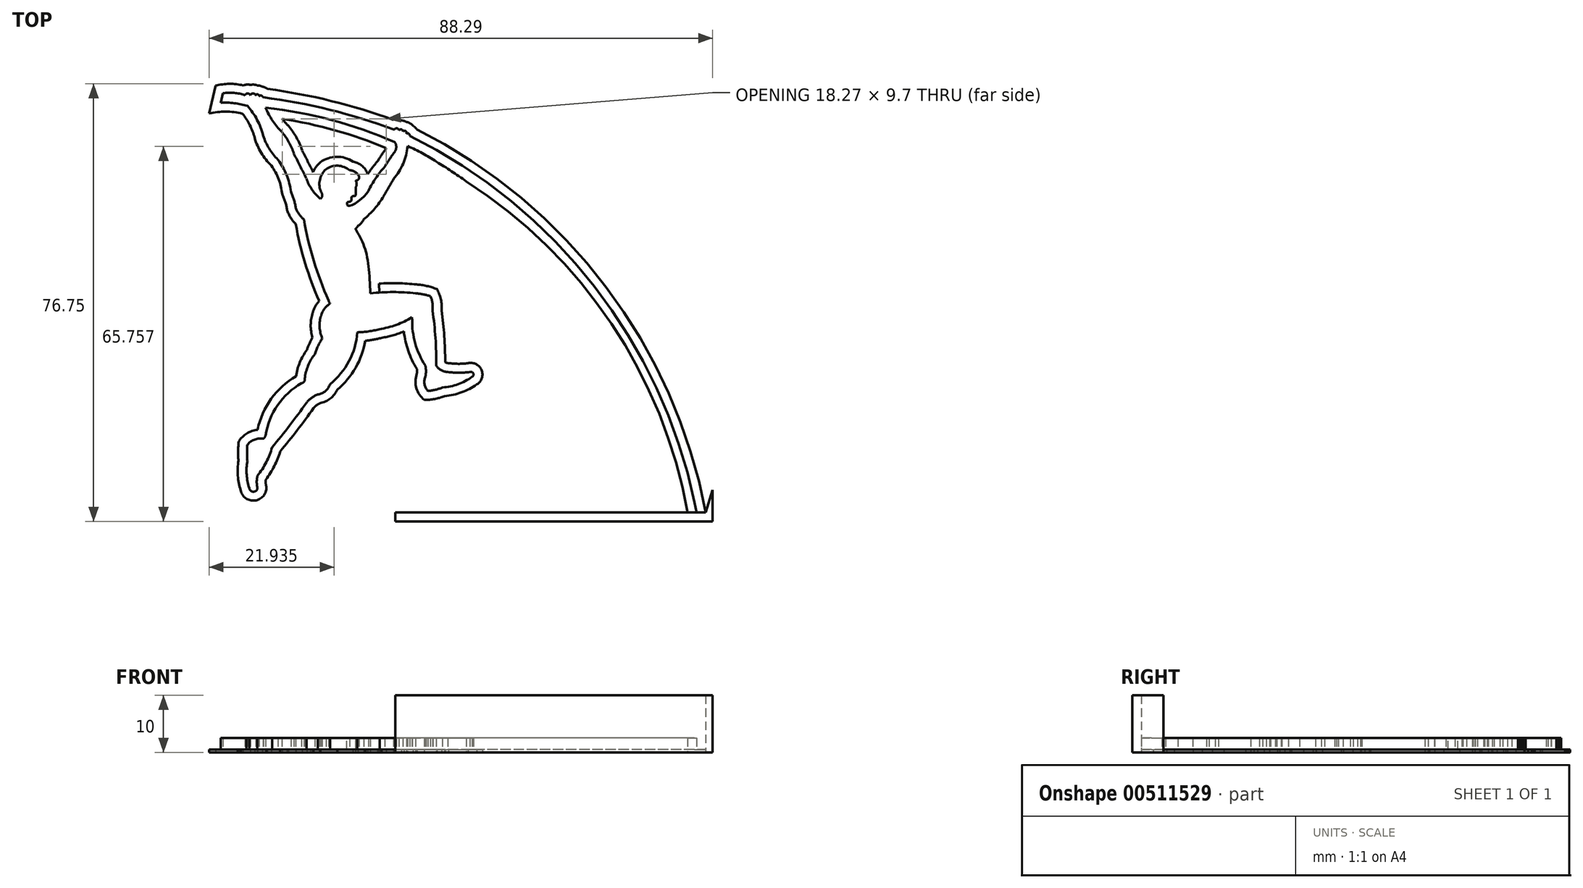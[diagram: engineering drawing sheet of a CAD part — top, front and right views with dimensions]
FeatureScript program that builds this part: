
annotation { "Feature Type Name" : "Feature", "Feature Type Description" : "" }
export const myFeature = defineFeature(function(context is Context, id is Id, definition is map)
    precondition{}
    {
        {
            var Q0;
            Q0=qCreatedBy(makeId("Top.planeOp"),FACE);
            var sketch = newSketch(context, id + "F0", { "sketchPlane" : qUnion([Q0])});
            skArc(sketch, "E0", {"start": v(-35.16, 43.56) * mm, "mid": v(-37.47, 44.04) * mm, "end": v(-39.82, 44.1) * mm});
            skArc(sketch, "E1", {"start": v(-35.6, 45.44) * mm, "mid": v(-37.5, 45.84) * mm, "end": v(-39.44, 45.77) * mm});
            skArc(sketch, "E2", {"start": v(-9.39, 39.38) * mm, "mid": v(-20.75, 42.89) * mm, "end": v(-32.43, 45.06) * mm});
            skArc(sketch, "E3", {"start": v(-9.38, 37.25) * mm, "mid": v(-20.44, 41.08) * mm, "end": v(-31.94, 43.24) * mm});
            skLineSegment(sketch, "E4", {"start": v(-39.82, 44.1) * mm, "end": v(-39.44, 45.77) * mm});
            skArc(sketch, "E5", {"start": v(43.25, -25.95) * mm, "mid": v(25.65, 11.92) * mm, "end": v(-6.7, 38.32) * mm});
            skArc(sketch, "E6", {"start": v(-33.7, 45.44) * mm, "mid": v(-34.17, 45.73) * mm, "end": v(-34.65, 45.44) * mm});
            skArc(sketch, "E7", {"start": v(-33.1, 45.27) * mm, "mid": v(-33.33, 45.57) * mm, "end": v(-33.7, 45.44) * mm});
            skArc(sketch, "E8", {"start": v(-32.43, 45.06) * mm, "mid": v(-32.7, 45.37) * mm, "end": v(-33.1, 45.27) * mm});
            skArc(sketch, "E9", {"start": v(-34.65, 45.44) * mm, "mid": v(-35.12, 45.73) * mm, "end": v(-35.6, 45.44) * mm});
            skArc(sketch, "E10", {"start": v(-32.38, 38.34) * mm, "mid": v(-33.46, 41.11) * mm, "end": v(-35.16, 43.56) * mm});
            skArc(sketch, "E11", {"start": v(-32.38, 38.34) * mm, "mid": v(-31.35, 36.06) * mm, "end": v(-29.8, 34.1) * mm});
            skArc(sketch, "E12", {"start": v(-31.94, 43.24) * mm, "mid": v(-30.76, 40.97) * mm, "end": v(-29.12, 39) * mm});
            skArc(sketch, "E13", {"start": v(-27, 35.16) * mm, "mid": v(-27.88, 37.18) * mm, "end": v(-29.12, 39) * mm});
            skArc(sketch, "E14", {"start": v(-24.81, 30.82) * mm, "mid": v(-25.9, 32.99) * mm, "end": v(-27, 35.16) * mm});
            skArc(sketch, "E15", {"start": v(-24.81, 30.82) * mm, "mid": v(-23.82, 28.85) * mm, "end": v(-22.34, 27.22) * mm});
            skArc(sketch, "E16", {"start": v(-27.53, 28.5) * mm, "mid": v(-28.29, 31.45) * mm, "end": v(-29.8, 34.1) * mm});
            skArc(sketch, "E17", {"start": v(-26.66, 25.66) * mm, "mid": v(-27, 27.1) * mm, "end": v(-27.53, 28.5) * mm});
            skArc(sketch, "E18", {"start": v(-26.66, 25.66) * mm, "mid": v(-26.1, 24.55) * mm, "end": v(-25.24, 23.63) * mm});
            skArc(sketch, "E19", {"start": v(-22.34, 27.22) * mm, "mid": v(-22.04, 27.8) * mm, "end": v(-22.22, 28.43) * mm});
            skArc(sketch, "E20", {"start": v(-21.38, 32.44) * mm, "mid": v(-22.46, 30.58) * mm, "end": v(-22.22, 28.43) * mm});
            skArc(sketch, "E21", {"start": v(-17.24, 32.26) * mm, "mid": v(-19.28, 33.06) * mm, "end": v(-21.38, 32.44) * mm});
            skArc(sketch, "E22", {"start": v(-15.57, 31.17) * mm, "mid": v(-16.24, 31.96) * mm, "end": v(-17.24, 32.26) * mm});
            skArc(sketch, "E23", {"start": v(-16.16, 30.45) * mm, "mid": v(-15.68, 30.66) * mm, "end": v(-15.57, 31.17) * mm});
            skArc(sketch, "E24", {"start": v(-16.16, 29.27) * mm, "mid": v(-16, 29.86) * mm, "end": v(-16.16, 30.45) * mm});
            skLineSegment(sketch, "E25", {"start": v(-16.16, 29.27) * mm, "end": v(-16.16, 28.39) * mm});
            skFitSpline(sketch, "E26", {"points": [v(-16.16, 28.39) * mm, v(-16.24, 27.77) * mm, v(-16.82, 27.66) * mm, v(-17.03, 26.84) * mm, v(-17.62, 26.64) * mm, v(-17.5, 26.04) * mm, v(-13.93, 28.66) * mm], "startDerivative": vector(-0.04, -4.98) * mm, "endDerivative": vector(6, 10.29) * mm});
            skArc(sketch, "E27", {"start": v(-11.07, 32.9) * mm, "mid": v(-12.66, 30.88) * mm, "end": v(-13.93, 28.66) * mm});
            skArc(sketch, "E28", {"start": v(-9.26, 35.62) * mm, "mid": v(-10.2, 34.28) * mm, "end": v(-11.07, 32.9) * mm});
            skArc(sketch, "E29", {"start": v(-9.26, 35.62) * mm, "mid": v(-9.06, 36.46) * mm, "end": v(-9.38, 37.25) * mm});
            skArc(sketch, "E30", {"start": v(-9.53, 30.73) * mm, "mid": v(-7.85, 33.42) * mm, "end": v(-7.05, 36.49) * mm});
            skArc(sketch, "E31", {"start": v(-9.53, 30.73) * mm, "mid": v(-10.41, 29.22) * mm, "end": v(-11.29, 27.71) * mm});
            skArc(sketch, "E32", {"start": v(-14.77, 23.67) * mm, "mid": v(-12.85, 25.53) * mm, "end": v(-11.29, 27.71) * mm});
            skArc(sketch, "E33", {"start": v(-15.79, 22.53) * mm, "mid": v(-15.2, 23.02) * mm, "end": v(-14.77, 23.67) * mm});
            skArc(sketch, "E34", {"start": v(-16.23, 22.01) * mm, "mid": v(-15.96, 22.23) * mm, "end": v(-15.79, 22.53) * mm});
            skFitSpline(sketch, "E35", {"points": [v(-16.23, 22.01) * mm, v(-14.37, 17.93) * mm, v(-13.6, 10.67) * mm], "startDerivative": vector(4.86, -8.48) * mm, "endDerivative": vector(0.59, -13.97) * mm});
            skArc(sketch, "E36", {"start": v(-5.65, 10.67) * mm, "mid": v(-9.62, 10.9) * mm, "end": v(-13.6, 10.67) * mm});
            skArc(sketch, "E37", {"start": v(-3.05, 10.17) * mm, "mid": v(-4.33, 10.5) * mm, "end": v(-5.65, 10.67) * mm});
            skArc(sketch, "E38", {"start": v(-2.7, 7.65) * mm, "mid": v(-2.7, 8.94) * mm, "end": v(-3.05, 10.17) * mm});
            skArc(sketch, "E39", {"start": v(-2.06, -1.97) * mm, "mid": v(-2.18, 2.85) * mm, "end": v(-2.7, 7.65) * mm});
            skArc(sketch, "E40", {"start": v(-2.06, -1.97) * mm, "mid": v(-1.17, -2.8) * mm, "end": v(0, -3.13) * mm});
            skArc(sketch, "E41", {"start": v(0, -3.13) * mm, "mid": v(1.92, -3.24) * mm, "end": v(3.84, -3.13) * mm});
            skArc(sketch, "E42", {"start": v(4.24, -3.96) * mm, "mid": v(4.44, -3.35) * mm, "end": v(3.84, -3.13) * mm});
            skArc(sketch, "E43", {"start": v(-0.94, -5.81) * mm, "mid": v(1.78, -5.26) * mm, "end": v(4.24, -3.96) * mm});
            skArc(sketch, "E44", {"start": v(-3.53, -6.44) * mm, "mid": v(-2.2, -6.24) * mm, "end": v(-0.94, -5.81) * mm});
            skArc(sketch, "E45", {"start": v(-3.98, -3.96) * mm, "mid": v(-4.1, -5.26) * mm, "end": v(-3.53, -6.44) * mm});
            skArc(sketch, "E46", {"start": v(-3.98, -3.96) * mm, "mid": v(-3.85, -2.97) * mm, "end": v(-3.98, -1.97) * mm});
            skArc(sketch, "E47", {"start": v(-6.27, 6.14) * mm, "mid": v(-5.73, 1.91) * mm, "end": v(-3.98, -1.97) * mm});
            skArc(sketch, "E48", {"start": v(-6.3, 6.48) * mm, "mid": v(-6.29, 6.3) * mm, "end": v(-6.27, 6.14) * mm});
            skArc(sketch, "E49", {"start": v(-12, 4.4) * mm, "mid": v(-9.04, 5.16) * mm, "end": v(-6.3, 6.48) * mm});
            skArc(sketch, "E50", {"start": v(-15.88, 3.85) * mm, "mid": v(-13.92, 4) * mm, "end": v(-12, 4.4) * mm});
            skArc(sketch, "E51", {"start": v(-20.68, -5.25) * mm, "mid": v(-17.33, -1.2) * mm, "end": v(-15.88, 3.85) * mm});
            skArc(sketch, "E52", {"start": v(-22.82, -7.06) * mm, "mid": v(-21.5, -6.46) * mm, "end": v(-20.68, -5.25) * mm});
            skArc(sketch, "E53", {"start": v(-22.82, -7.06) * mm, "mid": v(-23.92, -7.65) * mm, "end": v(-24.81, -8.53) * mm});
            skArc(sketch, "E54", {"start": v(-30.82, -16.31) * mm, "mid": v(-27.74, -12.48) * mm, "end": v(-24.81, -8.53) * mm});
            skArc(sketch, "E55", {"start": v(-33.39, -21.3) * mm, "mid": v(-31.85, -18.94) * mm, "end": v(-30.82, -16.31) * mm});
            skArc(sketch, "E56", {"start": v(-33.39, -21.3) * mm, "mid": v(-33.52, -22.4) * mm, "end": v(-33.39, -23.5) * mm});
            skArc(sketch, "E57", {"start": v(-34.83, -23.5) * mm, "mid": v(-34.1, -24.11) * mm, "end": v(-33.39, -23.5) * mm});
            skArc(sketch, "E58", {"start": v(-35.16, -18.74) * mm, "mid": v(-35.28, -21.14) * mm, "end": v(-34.83, -23.5) * mm});
            skArc(sketch, "E59", {"start": v(-35.16, -15.86) * mm, "mid": v(-35.22, -17.3) * mm, "end": v(-35.16, -18.74) * mm});
            skArc(sketch, "E60", {"start": v(-32.34, -14.8) * mm, "mid": v(-33.89, -14.96) * mm, "end": v(-35.16, -15.86) * mm});
            skArc(sketch, "E61", {"start": v(-32.34, -14.8) * mm, "mid": v(-32.1, -14.55) * mm, "end": v(-31.98, -14.22) * mm});
            skArc(sketch, "E62", {"start": v(-25.66, -5.09) * mm, "mid": v(-29.86, -8.93) * mm, "end": v(-31.98, -14.22) * mm});
            skArc(sketch, "E63", {"start": v(-25.66, -5.09) * mm, "mid": v(-25.2, -4.8) * mm, "end": v(-25.1, -4.26) * mm});
            skArc(sketch, "E64", {"start": v(-23.33, 0) * mm, "mid": v(-24.51, -2) * mm, "end": v(-25.1, -4.26) * mm});
            skArc(sketch, "E65", {"start": v(-22.03, 2.78) * mm, "mid": v(-22.77, 1.43) * mm, "end": v(-23.33, 0) * mm});
            skArc(sketch, "E66", {"start": v(-22.21, 6.83) * mm, "mid": v(-22.5, 4.79) * mm, "end": v(-22.03, 2.78) * mm});
            skArc(sketch, "E67", {"start": v(-20.66, 8.9) * mm, "mid": v(-21.63, 8) * mm, "end": v(-22.21, 6.83) * mm});
            skArc(sketch, "E68", {"start": v(-20.9, 9.43) * mm, "mid": v(-20.83, 9.14) * mm, "end": v(-20.66, 8.9) * mm});
            skArc(sketch, "E69", {"start": v(-8.58, 39.22) * mm, "mid": v(-8.92, 39.62) * mm, "end": v(-9.39, 39.38) * mm});
            skArc(sketch, "E70", {"start": v(-7.9, 39.06) * mm, "mid": v(-8.16, 39.43) * mm, "end": v(-8.58, 39.22) * mm});
            skArc(sketch, "E71", {"start": v(-7.27, 38.7) * mm, "mid": v(-7.43, 39.16) * mm, "end": v(-7.9, 39.06) * mm});
            skArc(sketch, "E72", {"start": v(-6.7, 38.32) * mm, "mid": v(-6.87, 38.7) * mm, "end": v(-7.27, 38.7) * mm});
            skLineSegment(sketch, "E73", {"start": v(-27, 35.16) * mm, "end": v(-27, 35.16) * mm});
            skArc(sketch, "E74", {"start": v(-25.24, 23.63) * mm, "mid": v(-23.53, 16.4) * mm, "end": v(-20.9, 9.43) * mm});
            skArc(sketch, "E75.0", {"start": v(45.2, -27.76) * mm, "mid": v(27.74, 11.77) * mm, "end": v(-5.45, 39.44) * mm});
            skArc(sketch, "E75.2", {"start": v(40.77, -27.76) * mm, "mid": v(23.91, 8.03) * mm, "end": v(-6, 33.93) * mm});
            skArc(sketch, "E75.3", {"start": v(-8.25, 29.82) * mm, "mid": v(-6.92, 31.77) * mm, "end": v(-6, 33.93) * mm});
            skArc(sketch, "E75.4", {"start": v(-8.25, 29.82) * mm, "mid": v(-9.1, 28.38) * mm, "end": v(-9.94, 26.93) * mm});
            skArc(sketch, "E75.5", {"start": v(-13.54, 22.66) * mm, "mid": v(-11.55, 24.64) * mm, "end": v(-9.94, 26.93) * mm});
            skArc(sketch, "E75.6", {"start": v(-14.28, 21.73) * mm, "mid": v(-13.87, 22.17) * mm, "end": v(-13.54, 22.66) * mm});
            skFitSpline(sketch, "E75.7", {"points": [v(-14.88, 22.79) * mm, v(-14.67, 22.44) * mm, v(-14.26, 21.7) * mm, v(-13.64, 20.5) * mm, v(-13.17, 19.37) * mm, v(-12.86, 18.37) * mm, v(-12.6, 17.32) * mm, v(-12.38, 15.96) * mm, v(-12.21, 14.25) * mm, v(-12.1, 12.5) * mm, v(-12.06, 11.32) * mm, v(-12.03, 10.74) * mm]});
            skArc(sketch, "E75.8", {"start": v(-5.5, 12.23) * mm, "mid": v(-8.8, 12.46) * mm, "end": v(-12.1, 12.38) * mm});
            skArc(sketch, "E75.9", {"start": v(-24.73, 0.74) * mm, "mid": v(-25.96, -1.43) * mm, "end": v(-26.62, -3.84) * mm});
            skArc(sketch, "E75.10", {"start": v(-23.75, 2.95) * mm, "mid": v(-24.3, 1.87) * mm, "end": v(-24.73, 0.74) * mm});
            skArc(sketch, "E75.11", {"start": v(-23.7, 7.29) * mm, "mid": v(-24.06, 5.12) * mm, "end": v(-23.75, 2.95) * mm});
            skArc(sketch, "E75.12", {"start": v(-22.57, 9.32) * mm, "mid": v(-23.25, 8.37) * mm, "end": v(-23.7, 7.29) * mm});
            skArc(sketch, "E75.13", {"start": v(-26.7, 22.84) * mm, "mid": v(-25.03, 15.96) * mm, "end": v(-22.57, 9.32) * mm});
            skArc(sketch, "E75.14", {"start": v(-28.19, 25.3) * mm, "mid": v(-27.59, 23.98) * mm, "end": v(-26.7, 22.84) * mm});
            skArc(sketch, "E75.15", {"start": v(-28.19, 25.3) * mm, "mid": v(-28.51, 26.71) * mm, "end": v(-29.05, 28.06) * mm});
            skArc(sketch, "E75.16", {"start": v(-29.05, 28.06) * mm, "mid": v(-29.67, 30.7) * mm, "end": v(-30.97, 33.08) * mm});
            skArc(sketch, "E75.17", {"start": v(-33.88, 37.92) * mm, "mid": v(-32.73, 35.32) * mm, "end": v(-30.97, 33.08) * mm});
            skArc(sketch, "E75.18", {"start": v(-33.88, 37.92) * mm, "mid": v(-34.73, 40.17) * mm, "end": v(-36.04, 42.18) * mm});
            skArc(sketch, "E75.19", {"start": v(-36.04, 42.18) * mm, "mid": v(-38.95, 42.56) * mm, "end": v(-41.87, 42.2) * mm});
            skLineSegment(sketch, "E75.20", {"start": v(-41.87, 42.2) * mm, "end": v(-40.73, 47.1) * mm});
            skArc(sketch, "E75.21", {"start": v(-8.15, 41) * mm, "mid": v(-8.85, 41.19) * mm, "end": v(-9.57, 41.11) * mm});
            skArc(sketch, "E75.22", {"start": v(-7.27, 40.74) * mm, "mid": v(-7.7, 40.93) * mm, "end": v(-8.15, 41) * mm});
            skArc(sketch, "E75.23", {"start": v(-6.12, 40.06) * mm, "mid": v(-6.63, 40.5) * mm, "end": v(-7.27, 40.74) * mm});
            skArc(sketch, "E75.24", {"start": v(-5.45, 39.44) * mm, "mid": v(-5.75, 39.8) * mm, "end": v(-6.12, 40.06) * mm});
            skArc(sketch, "E75.25", {"start": v(-9.57, 41.11) * mm, "mid": v(-20.44, 44.42) * mm, "end": v(-31.62, 46.53) * mm});
            skArc(sketch, "E75.26", {"start": v(-31.62, 46.53) * mm, "mid": v(-32.05, 46.79) * mm, "end": v(-32.53, 46.92) * mm});
            skArc(sketch, "E75.27", {"start": v(-32.53, 46.92) * mm, "mid": v(-32.96, 47.1) * mm, "end": v(-33.42, 47.15) * mm});
            skArc(sketch, "E75.28", {"start": v(-33.42, 47.15) * mm, "mid": v(-34.01, 47.28) * mm, "end": v(-34.63, 47.24) * mm});
            skArc(sketch, "E75.29", {"start": v(-34.63, 47.24) * mm, "mid": v(-35.26, 47.3) * mm, "end": v(-35.89, 47.15) * mm});
            skArc(sketch, "E75.30", {"start": v(-35.89, 47.15) * mm, "mid": v(-38.31, 47.43) * mm, "end": v(-40.73, 47.1) * mm});
            skArc(sketch, "E75.31", {"start": v(-26.62, -3.84) * mm, "mid": v(-31, -7.83) * mm, "end": v(-33.39, -13.24) * mm});
            skArc(sketch, "E75.32", {"start": v(-33.39, -13.24) * mm, "mid": v(-35.26, -13.9) * mm, "end": v(-36.68, -15.3) * mm});
            skArc(sketch, "E75.33", {"start": v(-36.68, -15.3) * mm, "mid": v(-36.78, -16.98) * mm, "end": v(-36.73, -18.67) * mm});
            skArc(sketch, "E75.34", {"start": v(-36.73, -18.67) * mm, "mid": v(-36.84, -21.3) * mm, "end": v(-36.34, -23.88) * mm});
            skArc(sketch, "E75.35", {"start": v(-36.34, -23.88) * mm, "mid": v(-33.82, -25.66) * mm, "end": v(-31.82, -23.31) * mm});
            skArc(sketch, "E75.36", {"start": v(-31.93, -21.97) * mm, "mid": v(-31.94, -22.65) * mm, "end": v(-31.82, -23.31) * mm});
            skArc(sketch, "E75.37", {"start": v(-31.93, -21.97) * mm, "mid": v(-30.45, -19.63) * mm, "end": v(-29.4, -17.06) * mm});
            skArc(sketch, "E75.38", {"start": v(-29.4, -17.06) * mm, "mid": v(-26.41, -13.31) * mm, "end": v(-23.55, -9.46) * mm});
            skArc(sketch, "E75.39", {"start": v(-22.4, -8.58) * mm, "mid": v(-23.04, -8.94) * mm, "end": v(-23.55, -9.46) * mm});
            skArc(sketch, "E75.40", {"start": v(-22.4, -8.58) * mm, "mid": v(-20.6, -7.75) * mm, "end": v(-19.38, -6.2) * mm});
            skArc(sketch, "E75.41", {"start": v(-19.38, -6.2) * mm, "mid": v(-16.18, -2.35) * mm, "end": v(-14.5, 2.36) * mm});
            skArc(sketch, "E75.42", {"start": v(-14.5, 2.36) * mm, "mid": v(-13.07, 2.56) * mm, "end": v(-11.66, 2.88) * mm});
            skArc(sketch, "E75.43", {"start": v(-11.66, 2.88) * mm, "mid": v(-9.66, 3.31) * mm, "end": v(-7.73, 4) * mm});
            skArc(sketch, "E75.44", {"start": v(-7.73, 4) * mm, "mid": v(-6.95, 0.58) * mm, "end": v(-5.44, -2.58) * mm});
            skArc(sketch, "E75.45", {"start": v(-5.48, -3.5) * mm, "mid": v(-5.41, -3.04) * mm, "end": v(-5.44, -2.58) * mm});
            skArc(sketch, "E75.46", {"start": v(-5.48, -3.5) * mm, "mid": v(-5.53, -5.98) * mm, "end": v(-4.12, -8.02) * mm});
            skArc(sketch, "E75.47", {"start": v(-4.12, -8.02) * mm, "mid": v(-2.32, -7.86) * mm, "end": v(-0.57, -7.35) * mm});
            skArc(sketch, "E75.48", {"start": v(-0.57, -7.35) * mm, "mid": v(2.4, -6.7) * mm, "end": v(5.09, -5.28) * mm});
            skArc(sketch, "E75.49", {"start": v(5.09, -5.28) * mm, "mid": v(5.89, -2.76) * mm, "end": v(3.51, -1.6) * mm});
            skArc(sketch, "E75.50", {"start": v(0.1, -1.57) * mm, "mid": v(1.8, -1.68) * mm, "end": v(3.51, -1.6) * mm});
            skArc(sketch, "E75.51", {"start": v(-0.49, -1.38) * mm, "mid": v(-0.2, -1.52) * mm, "end": v(0.1, -1.57) * mm});
            skArc(sketch, "E75.52", {"start": v(-0.49, -1.38) * mm, "mid": v(-0.64, 3.15) * mm, "end": v(-1.13, 7.67) * mm});
            skArc(sketch, "E75.53", {"start": v(-1.13, 7.67) * mm, "mid": v(-1.23, 9.62) * mm, "end": v(-1.95, 11.43) * mm});
            skArc(sketch, "E75.54", {"start": v(-1.95, 11.43) * mm, "mid": v(-3.7, 11.97) * mm, "end": v(-5.5, 12.23) * mm});
            skArc(sketch, "E76.0", {"start": v(-22.35, 33.67) * mm, "mid": v(-23.09, 32.89) * mm, "end": v(-23.64, 31.97) * mm});
            skArc(sketch, "E76.1", {"start": v(-16.64, 33.77) * mm, "mid": v(-19.51, 34.63) * mm, "end": v(-22.35, 33.67) * mm});
            skArc(sketch, "E76.2", {"start": v(-23.64, 31.97) * mm, "mid": v(-24.6, 33.86) * mm, "end": v(-25.55, 35.75) * mm});
            skArc(sketch, "E76.3", {"start": v(-14.1, 31.71) * mm, "mid": v(-15.1, 33.07) * mm, "end": v(-16.64, 33.77) * mm});
            skArc(sketch, "E76.4", {"start": v(-14.06, 31.59) * mm, "mid": v(-14.08, 31.65) * mm, "end": v(-14.1, 31.71) * mm});
            skArc(sketch, "E76.5", {"start": v(-12.33, 33.84) * mm, "mid": v(-13.24, 32.75) * mm, "end": v(-14.06, 31.59) * mm});
            skArc(sketch, "E76.6", {"start": v(-25.55, 35.75) * mm, "mid": v(-26.56, 38.03) * mm, "end": v(-27.98, 40.08) * mm});
            skArc(sketch, "E76.7", {"start": v(-29.07, 41.28) * mm, "mid": v(-28.55, 40.66) * mm, "end": v(-27.98, 40.08) * mm});
            skArc(sketch, "E76.8", {"start": v(-10.8, 36.15) * mm, "mid": v(-19.78, 39.28) * mm, "end": v(-29.07, 41.28) * mm});
            skArc(sketch, "E76.9", {"start": v(-10.8, 36.15) * mm, "mid": v(-11.58, 35.01) * mm, "end": v(-12.33, 33.84) * mm});
            skLineSegment(sketch, "E77", {"start": v(40.77, -27.76) * mm, "end": v(45.2, -27.76) * mm});
            skLineSegment(sketch, "E78", {"start": v(45.2, -27.76) * mm, "end": v(46.42, -23.83) * mm});
            skLineSegment(sketch, "E79", {"start": v(46.42, -23.83) * mm, "end": v(46.42, -27.76) * mm});
            skLineSegment(sketch, "E80", {"start": v(-9.23, -27.76) * mm, "end": v(-9.23, -29.32) * mm});
            skLineSegment(sketch, "E81", {"start": v(-9.23, -29.32) * mm, "end": v(46.42, -29.32) * mm});
            skLineSegment(sketch, "E82", {"start": v(46.42, -29.32) * mm, "end": v(46.42, -27.76) * mm});
            skLineSegment(sketch, "E83", {"start": v(40.77, -27.76) * mm, "end": v(-9.23, -27.76) * mm});
            skLineSegment(sketch, "E84", {"start": v(43.25, -25.95) * mm, "end": v(43.63, -27.76) * mm});
            skArc(sketch, "E85", {"start": v(42.04, -27.76) * mm, "mid": v(28.68, 5.34) * mm, "end": v(3.2, 30.32) * mm});
            skArc(sketch, "E86", {"start": v(-2.03, 33.76) * mm, "mid": v(-4.48, 35.24) * mm, "end": v(-7.05, 36.49) * mm});
            skArc(sketch, "E87", {"start": v(3.2, 30.32) * mm, "mid": v(0.62, 32.1) * mm, "end": v(-2.03, 33.76) * mm});
            skSolve(sketch);
        }
        {
            var Q0;
            Q0=makeQuery(id+"F0.imprint","IMPRINT",FACE,{"disambiguationData":[TD([[makeQuery(id+"F0.imprint","IMPRINT",EDGE,{"derivedFrom":sQuery(id+"F0.wireOp",EDGE,"E0")}),-1.0]])]});
            extrude(context, id + "F1", {"entities" : qUnion([Q0]), "depth" : 2.5 * mm, "offsetDistance" : 25.4 * mm});
        }
        {
            var Q0;
            Q0=makeQuery(id+"F0.imprint","IMPRINT",FACE,{"disambiguationData":[TD([[makeQuery(id+"F0.imprint","IMPRINT",EDGE,{"derivedFrom":sQuery(id+"F0.wireOp",EDGE,"E3")}),1.0]])]});
            var Q1;
            Q1=makeQuery(id+"F0.imprint","IMPRINT",FACE,{"disambiguationData":[TD([[makeQuery(id+"F0.imprint","IMPRINT",EDGE,{"derivedFrom":sQuery(id+"F0.wireOp",EDGE,"E0")}),1.0]])]});
            var Q2;
            Q2=makeQuery(id+"F0.imprint","IMPRINT",FACE,{"disambiguationData":[TD([[makeQuery(id+"F0.imprint","IMPRINT",EDGE,{"derivedFrom":sQuery(id+"F0.wireOp",EDGE,"E0")}),-1.0]])]});
            extrude(context, id + "F2", {"entities" : qUnion([Q0, Q1, Q2]), "operationType" : NewBodyOperationType.ADD, "depth" : .5 * mm, "offsetDistance" : 25.4 * mm});
        }
        {
            var Q0;
            Q0=makeQuery(id+"F0.imprint","IMPRINT",FACE,{"disambiguationData":[TD([[makeQuery(id+"F0.imprint","IMPRINT",EDGE,{"derivedFrom":sQuery(id+"F0.wireOp",EDGE,"E77")}),-1.0]])]});
            extrude(context, id + "F3", {"entities" : qUnion([Q0]), "operationType" : NewBodyOperationType.ADD, "depth" : 10 * mm, "offsetDistance" : 25.4 * mm});
        }
    });
